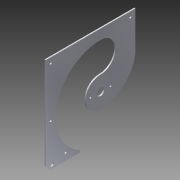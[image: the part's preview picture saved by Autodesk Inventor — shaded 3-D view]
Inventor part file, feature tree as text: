
AUTODESK INVENTOR PART (.ipt)
format: ipt  version: 2015 (Build 190159000, 159)  size: 222,208 bytes
history: native  units: in
note: dims shown in document units (in); Inventor stores cm internally (conversion verified against a paired STEP export)
features: sketch x6, projected_geometry x5, extrude x4, hole x2, fillet x1
ambient origin geometry x8: Origin, YZ Plane, XZ Plane, XY Plane, X Axis, Y Axis, Z Axis, Center Point
bodies: Solid1 (feature_tree)
feature tree (18):
  extrude  "Extrusion1"  Depth=2.5in
  extrude  "Extrusion2"  Depth=3.25in
  hole  "Hole1"  [1 undecoded]
  extrude  "Extrusion3"  Depth=9.0in
  extrude  "Extrusion4"  Depth=3.0in
  hole  "Hole3"  [1 undecoded]
  fillet  "Fillet1"  Radius=5.5in
  sketch  "Sketch1"  dims[d0=4.0in d1=2.5in]
  sketch  "Sketch2"  dims[d2=2.5in d3=3.25in]
  projected_geometry  "Projected Loop1"
  sketch  "Sketch3"  dims[d4=3.25in d5=0.0in]
  projected_geometry  "Projected Loop2"
  sketch  "Sketch4"  dims[d6=0.0in d7=9.0in]
  projected_geometry  "Projected Loop3"
  sketch  "Sketch5"  dims[d8=3.0in d9=3.0in]
  projected_geometry  "Projected Loop4"
  sketch  "Sketch6"  dims[d10=7.0in d11=3.5in d12=5.5in d13=0.0in d14=10.0in d15=5.5in d16=0.0in d17=2.3125in d18=4.0in d22=0.125in d23=0.0in d24=3.0in d25=0.25in d26=0.5in d27=0.125in d28=0.0in d29=0.5in d30=0.5in d31=0.5in d32=0.5in d33=0.5in d34=5.5in d35=3.5in d36=3.5in d37=0.25in d38=0.75in d39=0.375in d40=0.25in d41=0.5635in d42=1.0in d43=0.8108in d44=0.0in d45=0.0in d46=1.0in d47=1.0in d55=0.75in d56=0.1875in d57=0.1875in d58=0.125in d59=0.0in d60=0.5in d61=0.5in d62=0.125in d63=0.0in d64=0.625in d65=0.375in d66=0.375in d67=0.75in d68=0.375in d69=0.25in d70=0.5635in d71=1.0in d72=0.8108in d73=0.125in]
  projected_geometry  "Projected Loop5"
note: 2 required parameter values undecoded (feature->parameter linkage not recoverable at this tier; creation-order binding heuristic only, values carry confidence <= 0.55)
